# Revit family: Hekatron_Feststellanlagen_KONSOLE 143-K_DE_22.01
name_source: partatom
category: Brandmelder
revit_build: Autodesk Revit 2018 (Build: 20190510_1515(x64)
units: mm (PartAtom-declared; Revit-internal decimal feet)

## family parameters
Basisbauteil = Fläche
Beim Laden mit Abzugskörper schneiden = Nein
Bemaßung runder Anschluss = Durchmesser verwenden
Beschriftungsausrichtung beibehalten = Nein
Gemeinsam genutzt = Nein
Raumberechnungspunkt = Nein
Teiletyp = Normal

## types (1)
- Console 143-K
    Beschreibung = Konsole zur Montage von Rauch- und Thermoschaltern gemäß DIBt Vorgaben auf min. 3,5m über dem Türsturz bei Sturzhöhen größer 5m.
    Breite (mm) = 541.5
    Farbe = weiß, ähnlich RAL 9010
    Hersteller = Hekatron
    Höhe (mm) = 75.0
    Link zu Ausschreibungstext = https://www.meinhplus.de
    Link zu Produktinformation = https://www.hekatron-planungstools.de
    Link zu ausschreiben.de = http://www.ausschreiben.de
    Material = Metall
    Modell = KONSOLE 143-K
    Montageart = Wand- oder Sturzmontage
    Tiefe (mm) = 86.0
    Typenkommentare = Konsole für Montage der Krag- arm Rauch-und Thermoschalter
    UB A&S Artikel Nummer = 3510233
    URL = https://www.hekatron-brandschutz.de
    Version des BIM Objektes = 22.01
    Vorgabe-Ansicht = 1200 mm

## geometry (parser evidence)
native form markers: Sweep x2
no freeform markers — native parametric forms only
